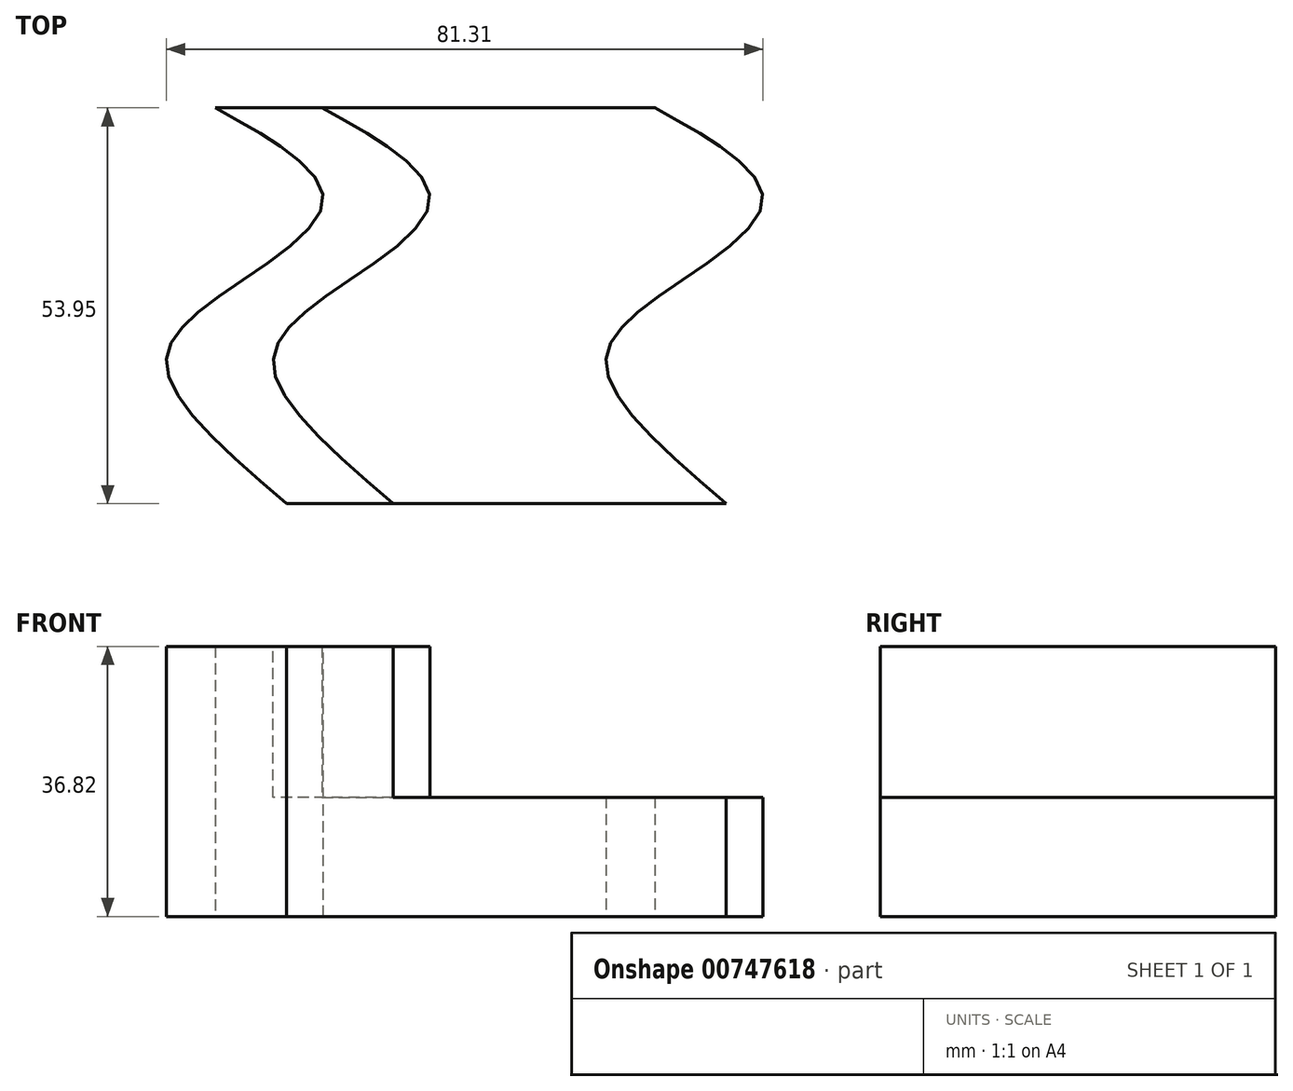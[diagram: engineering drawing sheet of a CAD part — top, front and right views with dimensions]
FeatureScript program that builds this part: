
annotation { "Feature Type Name" : "Feature", "Feature Type Description" : "" }
export const myFeature = defineFeature(function(context is Context, id is Id, definition is map)
    precondition{}
    {
        {
            var Q0;
            Q0=qCreatedBy(makeId("Front.planeOp"),FACE);
            var sketch = newSketch(context, id + "F0", { "sketchPlane" : qUnion([Q0])});
            skLineSegment(sketch, "E0.bottom", {"start": v(-42.96, 39.25) * mm, "end": v(-28.4, 39.25) * mm});
            skLineSegment(sketch, "E0.top", {"start": v(-42.96, 2.43) * mm, "end": v(-28.4, 2.43) * mm});
            skLineSegment(sketch, "E0.left", {"start": v(-42.96, 39.25) * mm, "end": v(-42.96, 2.43) * mm});
            skLineSegment(sketch, "E0.right", {"start": v(-28.4, 39.25) * mm, "end": v(-28.4, 18.7) * mm});
            skLineSegment(sketch, "E1.bottom", {"start": v(-28.4, 18.7) * mm, "end": v(16.98, 18.7) * mm});
            skLineSegment(sketch, "E1.top", {"start": v(-28.4, 2.43) * mm, "end": v(16.98, 2.43) * mm});
            skLineSegment(sketch, "E1.right", {"start": v(16.98, 18.7) * mm, "end": v(16.98, 2.43) * mm});
            skSolve(sketch);
        }
        {
            var Q0;
            Q0=qCreatedBy(makeId("Top.planeOp"),FACE);
            var sketch = newSketch(context, id + "F1", { "sketchPlane" : qUnion([Q0])});
            skFitSpline(sketch, "E2", {"points": [v(-14.7, 6.42) * mm, v(0, -6.42) * mm, v(-14.99, -19.84) * mm, v(-21.27, -29.26) * mm, v(-5, -47.53) * mm], "startDerivative": vector(88.67, -49.14) * mm, "endDerivative": vector(80.42, -68.65) * mm});
            skSolve(sketch);
        }
        {
            var Q0;
            Q0=makeQuery(id+"F0.imprint","IMPRINT",FACE,{"disambiguationData":[TD([[makeQuery(id+"F0.imprint","IMPRINT",EDGE,{"derivedFrom":sQuery(id+"F0.wireOp",EDGE,"E0.bottom")}),-1.0]])]});
            var Q1;
            Q1=sQuery(id+"F1.wireOp",EDGE,"E2");
            sweep(context, id + "F2", {"profiles" : qUnion([Q0]), "path" : qUnion([Q1]), "keepProfileOrientation" : true});
        }
    });
